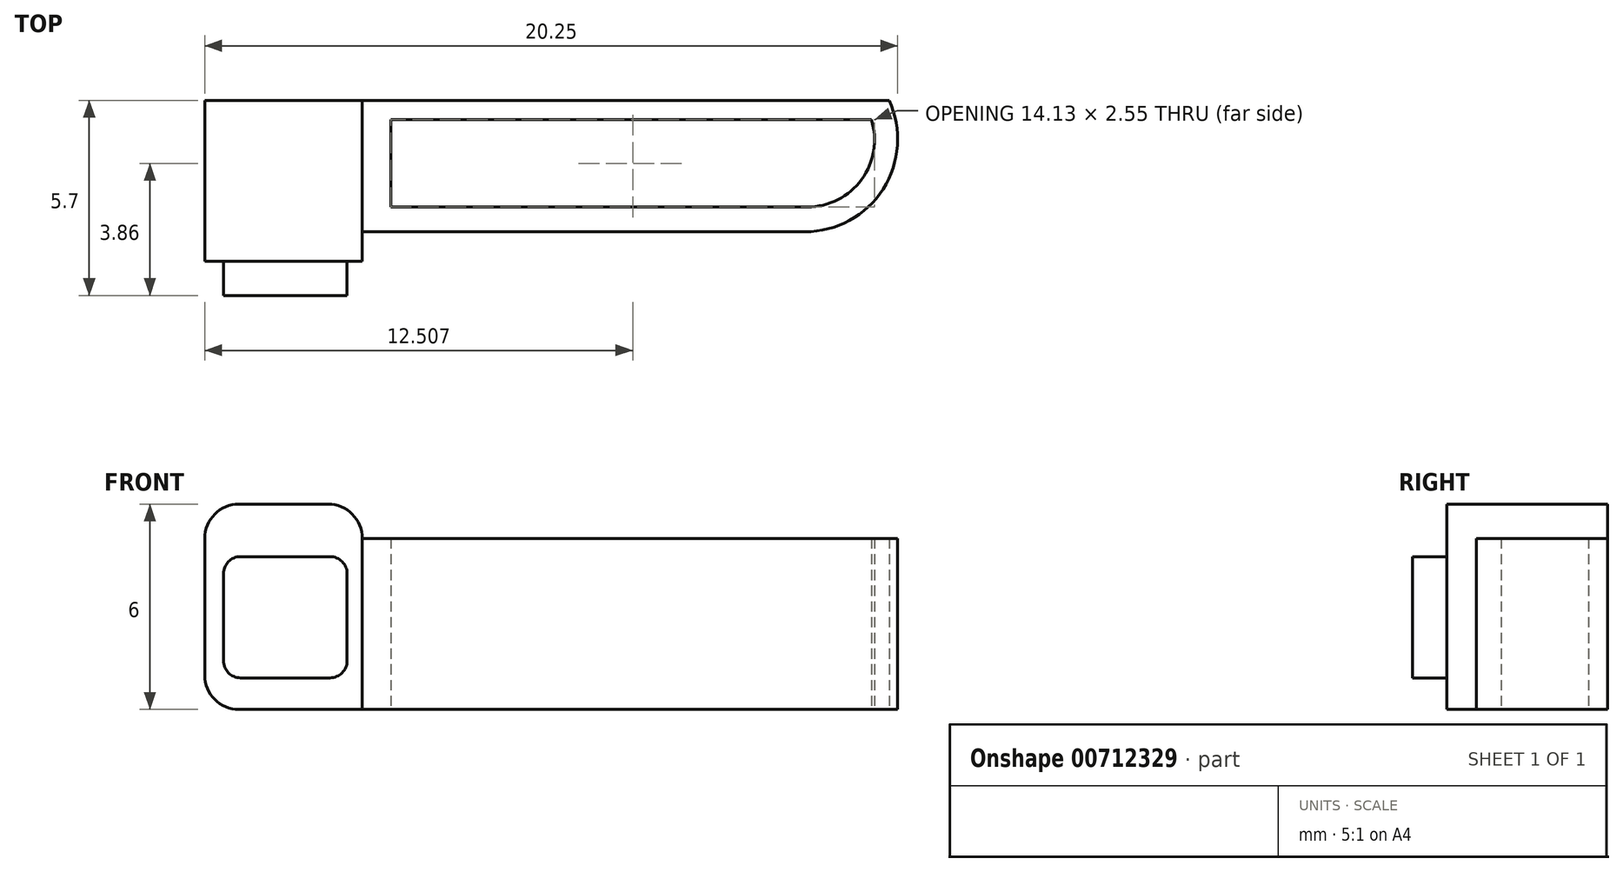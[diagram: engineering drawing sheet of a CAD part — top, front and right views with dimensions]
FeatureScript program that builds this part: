
annotation { "Feature Type Name" : "Feature", "Feature Type Description" : "" }
export const myFeature = defineFeature(function(context is Context, id is Id, definition is map)
    precondition{}
    {
        {
            var Q0;
            Q0=qCreatedBy(makeId("Top.planeOp"),FACE);
            var sketch = newSketch(context, id + "F0", { "sketchPlane" : qUnion([Q0])});
            skLineSegment(sketch, "E0", {"start": v(-11.53, 23.24) * mm, "end": v(8.47, 23.24) * mm});
            skLineSegment(sketch, "E1", {"start": v(-11.53, 23.24) * mm, "end": v(-11.53, 18.54) * mm});
            skLineSegment(sketch, "E2", {"start": v(-11.53, 18.54) * mm, "end": v(-6.92, 18.54) * mm});
            skLineSegment(sketch, "E3", {"start": v(-6.92, 18.54) * mm, "end": v(-6.92, 23.24) * mm});
            skLineSegment(sketch, "E4", {"start": v(-6.09, 22.67) * mm, "end": v(7.95, 22.67) * mm});
            skLineSegment(sketch, "E5", {"start": v(-6.09, 22.67) * mm, "end": v(-6.09, 20.13) * mm});
            skLineSegment(sketch, "E6", {"start": v(-6.92, 19.4) * mm, "end": v(6.01, 19.4) * mm});
            skLineSegment(sketch, "E7", {"start": v(-6.09, 20.13) * mm, "end": v(6.1, 20.13) * mm});
            skPoint(sketch, "E8.orphan", {"position": v(-6.09, 19.4) * mm});
            skArc(sketch, "E9", {"start": v(6.01, 19.4) * mm, "mid": v(8.3, 20.65) * mm, "end": v(8.47, 23.24) * mm});
            skArc(sketch, "E10", {"start": v(6.1, 20.13) * mm, "mid": v(7.67, 20.93) * mm, "end": v(7.95, 22.67) * mm});
            skPoint(sketch, "E11.end.orphan", {"position": v(-7.5, 22.67) * mm});
            skPoint(sketch, "E12.end.orphan", {"position": v(-11, 22.67) * mm});
            skPoint(sketch, "E12.start.orphan", {"position": v(-11, 19.08) * mm});
            skSolve(sketch);
        }
        {
            var Q0;
            Q0=makeQuery(id+"F0.imprint","IMPRINT",FACE,{"disambiguationData":[TD([[makeQuery(id+"F0.imprint","IMPRINT",EDGE,{"derivedFrom":sQuery(id+"F0.wireOp",EDGE,"E4")}),1.0]])]});
            extrude(context, id + "F1", {"entities" : qUnion([Q0]), "depth" : 5 * mm, "offsetDistance" : 25 * mm});
        }
        {
            var Q0;
            {var subQ5=sQuery(id+"F0.wireOp",EDGE,"E1");Q0=makeQuery(id+"F0.imprint","IMPRINT",FACE,{"disambiguationData":[TD([[makeQuery(id+"F0.imprint","IMPRINT",EDGE,{"derivedFrom":subQ5}),1.0]])]});}
            extrude(context, id + "F2", {"entities" : qUnion([Q0]), "operationType" : NewBodyOperationType.ADD, "depth" : 6 * mm, "offsetDistance" : 25 * mm});
        }
        {
            var Q0;
            Q0=makeQuery(id+"F2.opExtrude","SWEPT_FACE",FACE,{"disambiguationData":[OSD([sQuery(id+"F0.wireOp",EDGE,"E2")])]});
            var sketch = newSketch(context, id + "F3", { "sketchPlane" : qUnion([Q0])});
            skLineSegment(sketch, "E13.bottom", {"start": v(-10.98, 4.47) * mm, "end": v(-7.37, 4.47) * mm});
            skLineSegment(sketch, "E13.top", {"start": v(-10.98, 0.92) * mm, "end": v(-7.37, 0.92) * mm});
            skLineSegment(sketch, "E13.left", {"start": v(-10.98, 4.47) * mm, "end": v(-10.98, 0.92) * mm});
            skLineSegment(sketch, "E13.right", {"start": v(-7.37, 4.47) * mm, "end": v(-7.37, 0.92) * mm});
            skSolve(sketch);
        }
        {
            var Q0;
            Q0=makeQuery(id+"F3.imprint","IMPRINT",FACE,{"disambiguationData":[TD([[makeQuery(id+"F3.imprint","IMPRINT",EDGE,{"derivedFrom":sQuery(id+"F3.wireOp",EDGE,"E13.bottom")}),-1.0]])]});
            extrude(context, id + "F4", {"entities" : qUnion([Q0]), "operationType" : NewBodyOperationType.ADD, "depth" : 1 * mm, "offsetDistance" : 25 * mm});
        }
        {
            var Q0;
            Q0=makeQuery(id+"F2.opExtrude","CAP_EDGE",EDGE,{"disambiguationData":[OSD([sQuery(id+"F0.wireOp",EDGE,"E1")])],"isStart":false});
            var Q1;
            Q1=makeQuery(id+"F2.opExtrude","CAP_EDGE",EDGE,{"disambiguationData":[OSD([sQuery(id+"F0.wireOp",EDGE,"E3")])],"isStart":false});
            var Q2;
            Q2=makeQuery(id+"F2.opExtrude","CAP_EDGE",EDGE,{"disambiguationData":[OSD([sQuery(id+"F0.wireOp",EDGE,"E1")])],"isStart":true});
            fillet(context, id + "F5", {"entities" : qUnion([Q0, Q1, Q2]), "tangentPropagation" : true, "radius" : 1 * mm, "defaultsChanged" : false, "vertexSettings" : [], "allowEdgeOverflow" : false});
        }
        {
            var Q0;
            Q0=makeQuery(id+"F4.opExtrude","SWEPT_EDGE",EDGE,{"disambiguationData":[OSD([sQuery(id+"F3.wireOp",EDGE,"E13.bottom"),sQuery(id+"F3.wireOp",EDGE,"E13.left")])]});
            var Q1;
            Q1=makeQuery(id+"F4.opExtrude","SWEPT_EDGE",EDGE,{"disambiguationData":[OSD([sQuery(id+"F3.wireOp",EDGE,"E13.bottom"),sQuery(id+"F3.wireOp",EDGE,"E13.right")])]});
            var Q2;
            Q2=makeQuery(id+"F4.opExtrude","SWEPT_EDGE",EDGE,{"disambiguationData":[OSD([sQuery(id+"F3.wireOp",EDGE,"E13.top"),sQuery(id+"F3.wireOp",EDGE,"E13.left")])]});
            var Q3;
            Q3=makeQuery(id+"F4.opExtrude","SWEPT_EDGE",EDGE,{"disambiguationData":[OSD([sQuery(id+"F3.wireOp",EDGE,"E13.top"),sQuery(id+"F3.wireOp",EDGE,"E13.right")])]});
            fillet(context, id + "F6", {"entities" : qUnion([Q0, Q1, Q2, Q3]), "tangentPropagation" : true, "radius" : .5 * mm, "defaultsChanged" : false, "vertexSettings" : [], "allowEdgeOverflow" : false});
        }
    });
